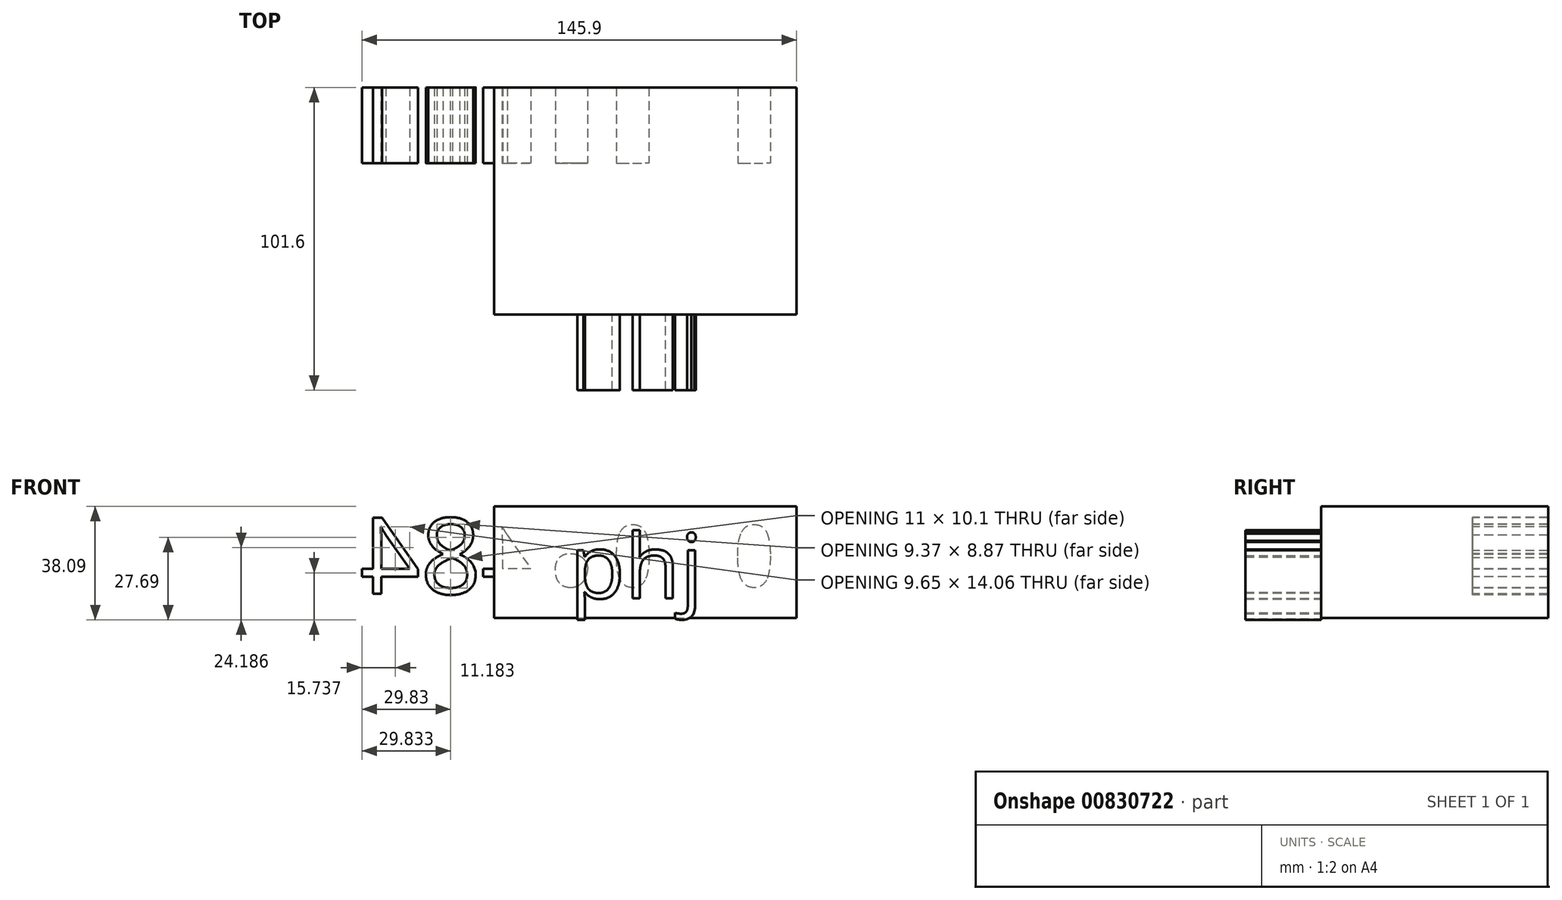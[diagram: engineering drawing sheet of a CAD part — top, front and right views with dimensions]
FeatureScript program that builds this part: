
annotation { "Feature Type Name" : "Feature", "Feature Type Description" : "" }
export const myFeature = defineFeature(function(context is Context, id is Id, definition is map)
    precondition{}
    {
        {
            var Q0;
            Q0=qCreatedBy(makeId("Front.planeOp"),FACE);
            var sketch = newSketch(context, id + "F0", { "sketchPlane" : qUnion([Q0])});
            skLineSegment(sketch, "E0.bottom", {"start": v(0, 0) * mm, "end": v(101.49, 0) * mm});
            skLineSegment(sketch, "E0.top", {"start": v(0, 37.52) * mm, "end": v(101.49, 37.52) * mm});
            skLineSegment(sketch, "E0.left", {"start": v(0, 0) * mm, "end": v(0, 37.52) * mm});
            skLineSegment(sketch, "E0.right", {"start": v(101.49, 0) * mm, "end": v(101.49, 37.52) * mm});
            skSolve(sketch);
        }
        {
            var Q0;
            Q0=makeQuery(id+"F0.imprint","IMPRINT",FACE,{"disambiguationData":[TD([[makeQuery(id+"F0.imprint","IMPRINT",EDGE,{"derivedFrom":sQuery(id+"F0.wireOp",EDGE,"E0.bottom")}),1.0]])]});
            extrude(context, id + "F1", {"entities" : qUnion([Q0]), "depth" : 50.8 * mm, "offsetDistance" : 25.4 * mm});
        }
        {
            var Q0;
            Q0=makeQuery(id+"F1.opExtrude","CAP_FACE",FACE,{"disambiguationData":[OSD([sQuery(id+"F0.wireOp",EDGE,"E0.bottom"),sQuery(id+"F0.wireOp",EDGE,"E0.top"),sQuery(id+"F0.wireOp",EDGE,"E0.left"),sQuery(id+"F0.wireOp",EDGE,"E0.right")])],"isStart":false});
            var sketch = newSketch(context, id + "F2", { "sketchPlane" : qUnion([Q0])});
            skText(sketch, "E1", { "text": "phj", "fontName": "OpenSans-Regular.ttf"});
            const initialGuessF2  = {"E1": [0.02538, 0.00667, 1, 0, 0.0217]};
            skSetInitialGuess(sketch, initialGuessF2);
            skSolve(sketch);
        }
        {
            var Q0;
            Q0=makeQuery(id+"F1.opExtrude","CAP_FACE",FACE,{"disambiguationData":[OSD([sQuery(id+"F0.wireOp",EDGE,"E0.bottom"),sQuery(id+"F0.wireOp",EDGE,"E0.top"),sQuery(id+"F0.wireOp",EDGE,"E0.left"),sQuery(id+"F0.wireOp",EDGE,"E0.right")])],"isStart":true});
            var sketch = newSketch(context, id + "F3", { "sketchPlane" : qUnion([Q0])});
            skText(sketch, "E2", { "text": "0106484", "fontName": "OpenSans-Regular.ttf"});
            const initialGuessF3  = {"E2": [-0.09734, 0.00812, 1, 0, 0.02563]};
            skSetInitialGuess(sketch, initialGuessF3);
            skSolve(sketch);
        }
        {
            var Q0;
            Q0=makeQuery(id+"F3.imprint","IMPRINT",FACE,{"disambiguationData":[TD([[makeQuery(id+"F3.imprint","IMPRINT",EDGE,{"derivedFrom":sQuery(id+"F3.wireOp",EDGE,"E2.sketch_text.stroke-0")}),1.0]])]});
            var Q1;
            Q1 = qSketchRegion(id + "F3", true);
            extrude(context, id + "F4", {"entities" : qUnion([Q0, Q1]), "operationType" : NewBodyOperationType.ADD, "depth" : 25.4 * mm, "offsetDistance" : 25.4 * mm});
        }
        {
            var Q0;
            Q0 = qSketchRegion(id + "F2", true);
            extrude(context, id + "F5", {"entities" : qUnion([Q0]), "operationType" : NewBodyOperationType.ADD, "depth" : 25.4 * mm, "offsetDistance" : 25.4 * mm});
        }
    });
